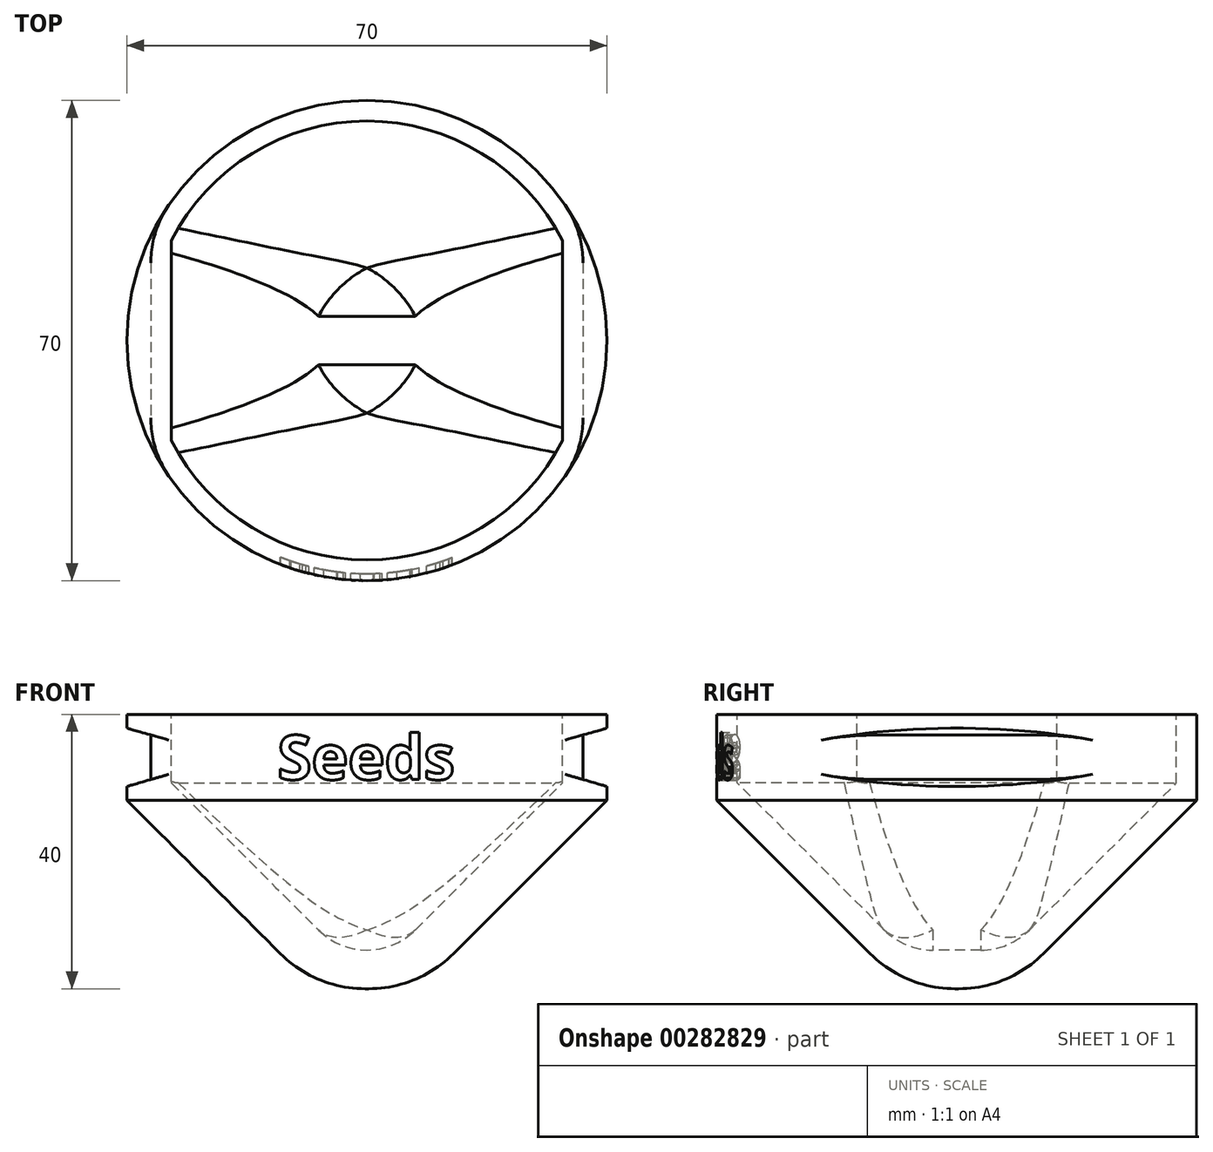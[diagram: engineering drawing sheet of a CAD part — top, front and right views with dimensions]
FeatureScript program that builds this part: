
annotation { "Feature Type Name" : "Feature", "Feature Type Description" : "" }
export const myFeature = defineFeature(function(context is Context, id is Id, definition is map)
    precondition{}
    {
        {
            var Q0;
            Q0=qCreatedBy(makeId("Top.planeOp"),FACE);
            var sketch = newSketch(context, id + "F0", { "sketchPlane" : qUnion([Q0])});
            skCircle(sketch, "E0", {"center": v(0, 0) * mm, "radius": 35 * mm});
            skSolve(sketch);
        }
        {
            var Q0;
            Q0=qSketchRegion(id+"F0",true);
            extrude(context, id + "F1", {"entities" : qUnion([Q0]), "depth" : 12.5 * mm});
        }
        {
            var Q0;
            Q0=qCreatedBy(makeId("Front.planeOp"),FACE);
            var sketch = newSketch(context, id + "F2", { "sketchPlane" : qUnion([Q0])});
            skText(sketch, "E1", { "text": "Seeds\n", "fontName": "OpenSans-Bold.ttf"});
            const initialGuessF2  = {"E1": [-0.01304, 0.003, 1, 0, 0.0065]};
            skSetInitialGuess(sketch, initialGuessF2);
            skSolve(sketch);
        }
        {
            var Q0;
            Q0=qSketchRegion(id+"F2",true);
            var Q1;
            Q1=makeQuery(id+"F1.opExtrude","SWEPT_FACE",FACE,{"disambiguationData":[OSD([sQuery(id+"F0.wireOp",EDGE,"E0")])]});
            extrude(context, id + "F3", {"entities" : qUnion([Q0]), "operationType" : NewBodyOperationType.REMOVE, "endBound" : BoundingType.THROUGH_ALL, "endBoundEntityFace" : qUnion([Q1]), "depth" : 25 * mm});
        }
        {
            var Q0;
            Q0=makeQuery(id+"F1.opExtrude","CAP_FACE",FACE,{"disambiguationData":[OSD([sQuery(id+"F0.wireOp",EDGE,"E0")])],"isStart":false});
            var sketch = newSketch(context, id + "F4", { "sketchPlane" : qUnion([Q0])});
            skCircle(sketch, "E2", {"center": v(0, 0) * mm, "radius": 34 * mm});
            skSolve(sketch);
        }
        {
            var Q0;
            Q0=qSketchRegion(id+"F4",true);
            var Q1;
            Q1=makeQuery(id+"F1.opExtrude","CAP_FACE",FACE,{"disambiguationData":[OSD([sQuery(id+"F0.wireOp",EDGE,"E0")])],"isStart":true});
            extrude(context, id + "F5", {"entities" : qUnion([Q0]), "operationType" : NewBodyOperationType.ADD, "endBound" : BoundingType.UP_TO_SURFACE, "oppositeDirection" : true, "endBoundEntityFace" : qUnion([Q1]), "depth" : 25 * mm});
        }
        {
            var Q0;
            Q0=qCreatedBy(makeId("Front.planeOp"),FACE);
            var sketch = newSketch(context, id + "F6", { "sketchPlane" : qUnion([Q0])});
            skLineSegment(sketch, "E3", {"start": v(-35, 10.5) * mm, "end": v(-35, 2) * mm});
            skLineSegment(sketch, "E4", {"start": v(-35, 2) * mm, "end": v(-31.5, 3) * mm});
            skLineSegment(sketch, "E5", {"start": v(-31.5, 3) * mm, "end": v(-31.5, 9.5) * mm});
            skLineSegment(sketch, "E6", {"start": v(-31.5, 9.5) * mm, "end": v(-35, 10.5) * mm});
            skLineSegment(sketch, "E7.MirrorCS", {"start": v(35, 10.5) * mm, "end": v(35, 2) * mm});
            skLineSegment(sketch, "E8.MirrorCS", {"start": v(31.5, 9.5) * mm, "end": v(35, 10.5) * mm});
            skLineSegment(sketch, "E9.MirrorCS", {"start": v(35, 2) * mm, "end": v(31.5, 3) * mm});
            skLineSegment(sketch, "E10.MirrorCS", {"start": v(31.5, 3) * mm, "end": v(31.5, 9.5) * mm});
            skSolve(sketch);
        }
        {
            var Q0;
            Q0=qSketchRegion(id+"F6",true);
            extrude(context, id + "F7", {"entities" : qUnion([Q0]), "operationType" : NewBodyOperationType.REMOVE, "endBound" : BoundingType.THROUGH_ALL, "oppositeDirection" : true, "depth" : 25 * mm, "hasSecondDirection" : true, "secondDirectionBound" : SecondDirectionBoundingType.THROUGH_ALL, "secondDirectionOppositeDirection" : false, "secondDirectionDepth" : 25 * mm});
        }
        {
            var Q0;
            {var subQ0=sQuery(id+"F0.wireOp",EDGE,"E0");Q0=makeQuery(id+"F7.boolean.opBoolean","INTERSECT",EDGE,{"disambiguationData":[OD(0.0)],"derivedFrom":[makeQuery(id+"F3.boolean.opBoolean","SPLIT",FACE,{"disambiguationData":[TD([makeQuery(id+"F1.opExtrude","CAP_FACE",FACE,{"disambiguationData":[OSD([subQ0])],"isStart":true})])],"derivedFrom":makeQuery(id+"F1.opExtrude","SWEPT_FACE",FACE,{"disambiguationData":[OSD([subQ0])]})}),makeQuery(id+"F7.opExtrude","SWEPT_FACE",FACE,{"disambiguationData":[OSD([sQuery(id+"F6.wireOp",EDGE,"E5")])]})]});}
            var Q1;
            {var subQ0=sQuery(id+"F0.wireOp",EDGE,"E0");Q1=makeQuery(id+"F7.boolean.opBoolean","INTERSECT",EDGE,{"disambiguationData":[OD(0.0)],"derivedFrom":[makeQuery(id+"F3.boolean.opBoolean","SPLIT",FACE,{"disambiguationData":[TD([makeQuery(id+"F1.opExtrude","CAP_FACE",FACE,{"disambiguationData":[OSD([subQ0])],"isStart":true})])],"derivedFrom":makeQuery(id+"F1.opExtrude","SWEPT_FACE",FACE,{"disambiguationData":[OSD([subQ0])]})}),makeQuery(id+"F7.opExtrude","SWEPT_FACE",FACE,{"disambiguationData":[OSD([sQuery(id+"F6.wireOp",EDGE,"E10.MirrorCS")])]})]});}
            var Q2;
            {var subQ0=sQuery(id+"F0.wireOp",EDGE,"E0");Q2=makeQuery(id+"F7.boolean.opBoolean","INTERSECT",EDGE,{"disambiguationData":[OD(1.0)],"derivedFrom":[makeQuery(id+"F3.boolean.opBoolean","SPLIT",FACE,{"disambiguationData":[TD([makeQuery(id+"F1.opExtrude","CAP_FACE",FACE,{"disambiguationData":[OSD([subQ0])],"isStart":true})])],"derivedFrom":makeQuery(id+"F1.opExtrude","SWEPT_FACE",FACE,{"disambiguationData":[OSD([subQ0])]})}),makeQuery(id+"F7.opExtrude","SWEPT_FACE",FACE,{"disambiguationData":[OSD([sQuery(id+"F6.wireOp",EDGE,"E10.MirrorCS")])]})]});}
            var Q3;
            {var subQ0=sQuery(id+"F0.wireOp",EDGE,"E0");Q3=makeQuery(id+"F7.boolean.opBoolean","INTERSECT",EDGE,{"disambiguationData":[OD(1.0)],"derivedFrom":[makeQuery(id+"F3.boolean.opBoolean","SPLIT",FACE,{"disambiguationData":[TD([makeQuery(id+"F1.opExtrude","CAP_FACE",FACE,{"disambiguationData":[OSD([subQ0])],"isStart":true})])],"derivedFrom":makeQuery(id+"F1.opExtrude","SWEPT_FACE",FACE,{"disambiguationData":[OSD([subQ0])]})}),makeQuery(id+"F7.opExtrude","SWEPT_FACE",FACE,{"disambiguationData":[OSD([sQuery(id+"F6.wireOp",EDGE,"E5")])]})]});}
            fillet(context, id + "F8", {"entities" : qUnion([Q0, Q1, Q2, Q3]), "radius" : 15 * mm, "tangentPropagation" : true, "allowEdgeOverflow" : false});
        }
        {
            var Q0;
            Q0=makeQuery(id+"F1.opExtrude","CAP_FACE",FACE,{"disambiguationData":[OSD([sQuery(id+"F0.wireOp",EDGE,"E0")])],"isStart":true});
            var sketch = newSketch(context, id + "F9", { "sketchPlane" : qUnion([Q0])});
            skCircle(sketch, "E11.0.0", {"center": v(0, 0) * mm, "radius": 35 * mm});
            skSolve(sketch);
        }
        {
            var Q0;
            Q0=qSketchRegion(id+"F9",true);
            extrude(context, id + "F10", {"entities" : qUnion([Q0]), "operationType" : NewBodyOperationType.ADD, "depth" : 27.5 * mm, "hasDraft" : true, "draftAngle" : 45 * degree, "draftPullDirection" : true});
        }
        {
            var Q0;
            Q0=makeQuery(id+"F1.opExtrude","CAP_FACE",FACE,{"disambiguationData":[OSD([sQuery(id+"F0.wireOp",EDGE,"E0")])],"isStart":false});
            var sketch = newSketch(context, id + "F11", { "sketchPlane" : qUnion([Q0])});
            skArc(sketch, "E12", {"start": v(-28.5, -14.55) * mm, "mid": v(0, -32) * mm, "end": v(28.5, -14.55) * mm});
            skLineSegment(sketch, "E13", {"start": v(-28.5, 14.55) * mm, "end": v(-28.5, -14.55) * mm});
            skLineSegment(sketch, "E14", {"start": v(28.5, 14.55) * mm, "end": v(28.5, -14.55) * mm});
            skArc(sketch, "E15.trimOffspring", {"start": v(28.5, 14.55) * mm, "mid": v(0, 32) * mm, "end": v(-28.5, 14.55) * mm});
            skSolve(sketch);
        }
        {
            var Q0;
            Q0=qSketchRegion(id+"F11",true);
            extrude(context, id + "F12", {"entities" : qUnion([Q0]), "operationType" : NewBodyOperationType.REMOVE, "oppositeDirection" : true, "depth" : 10 * mm});
        }
        {
            var Q0;
            Q0=makeQuery(id+"F12.boolean.opBoolean","COPY",FACE,{"derivedFrom":makeQuery(id+"F12.opExtrude","CAP_FACE",FACE,{"disambiguationData":[OSD([sQuery(id+"F11.wireOp",EDGE,"E12"),sQuery(id+"F11.wireOp",EDGE,"E13"),sQuery(id+"F11.wireOp",EDGE,"E14"),sQuery(id+"F11.wireOp",EDGE,"E15.trimOffspring")])],"isStart":false})});
            var sketch = newSketch(context, id + "F13", { "sketchPlane" : qUnion([Q0])});
            skArc(sketch, "E16.0", {"start": v(28.5, 14.55) * mm, "mid": v(0, 32) * mm, "end": v(-28.5, 14.55) * mm});
            skLineSegment(sketch, "E17.0", {"start": v(-28.5, 14.55) * mm, "end": v(-28.5, -14.55) * mm});
            skArc(sketch, "E17.1", {"start": v(-28.5, -14.55) * mm, "mid": v(0, -32) * mm, "end": v(28.5, -14.55) * mm});
            skLineSegment(sketch, "E17.2", {"start": v(28.5, 14.55) * mm, "end": v(28.5, -14.55) * mm});
            skSolve(sketch);
        }
        {
            var Q0;
            Q0=qSketchRegion(id+"F13",true);
            extrude(context, id + "F14", {"entities" : qUnion([Q0]), "operationType" : NewBodyOperationType.REMOVE, "endBound" : BoundingType.THROUGH_ALL, "oppositeDirection" : true, "depth" : 45 * mm, "hasDraft" : true, "draftAngle" : 45 * degree, "draftPullDirection" : true});
        }
        {
            var Q0;
            Q0=makeQuery(id+"F14.boolean.opBoolean","COPY",EDGE,{"derivedFrom":makeQuery(id+"F14.*.draft.opDraft","SPLIT",EDGE,{"derivedFrom":makeQuery(id+"F14.opExtrude","SWEPT_EDGE",EDGE,{"disambiguationData":[OSD([sQuery(id+"F13.wireOp",EDGE,"E16.0"),sQuery(id+"F13.wireOp",EDGE,"E17.0")])]})})});
            var Q1;
            {var subQ0=sQuery(id+"F13.wireOp",EDGE,"E17.2");var subQ1=sQuery(id+"F13.wireOp",EDGE,"E16.0");var subQ2=sQuery(id+"F13.wireOp",EDGE,"E17.0");var subQ3=sQuery(id+"F13.wireOp",EDGE,"E17.1");Q1=makeQuery(id+"F14.boolean.opBoolean","COPY",EDGE,{"derivedFrom":makeQuery(id+"F14.*.draft.opDraft","MERGE",EDGE,{"derivedFrom":[makeQuery(id+"F14.opExtrude","SWEPT_EDGE",EDGE,{"disambiguationData":[OSD([subQ2,subQ3])]}),makeQuery(id+"F14.opExtrude","SWEPT_EDGE",EDGE,{"disambiguationData":[OSD([subQ3,subQ0])]}),makeQuery(id+"F14.opExtrude","SWEPT_EDGE",EDGE,{"disambiguationData":[OSD([subQ1,subQ2])]}),makeQuery(id+"F14.opExtrude","SWEPT_EDGE",EDGE,{"disambiguationData":[OSD([subQ1,subQ0])]})]})});}
            var Q2;
            Q2=makeQuery(id+"F14.boolean.opBoolean","COPY",EDGE,{"derivedFrom":makeQuery(id+"F14.*.draft.opDraft","SPLIT",EDGE,{"derivedFrom":makeQuery(id+"F14.opExtrude","SWEPT_EDGE",EDGE,{"disambiguationData":[OSD([sQuery(id+"F13.wireOp",EDGE,"E16.0"),sQuery(id+"F13.wireOp",EDGE,"E17.2")])]})})});
            var Q3;
            Q3=makeQuery(id+"F14.boolean.opBoolean","COPY",EDGE,{"derivedFrom":makeQuery(id+"F14.*.draft.opDraft","SPLIT",EDGE,{"derivedFrom":makeQuery(id+"F14.opExtrude","SWEPT_EDGE",EDGE,{"disambiguationData":[OSD([sQuery(id+"F13.wireOp",EDGE,"E17.1"),sQuery(id+"F13.wireOp",EDGE,"E17.2")])]})})});
            var Q4;
            Q4=makeQuery(id+"F14.boolean.opBoolean","COPY",EDGE,{"derivedFrom":makeQuery(id+"F14.*.draft.opDraft","SPLIT",EDGE,{"derivedFrom":makeQuery(id+"F14.opExtrude","SWEPT_EDGE",EDGE,{"disambiguationData":[OSD([sQuery(id+"F13.wireOp",EDGE,"E17.0"),sQuery(id+"F13.wireOp",EDGE,"E17.1")])]})})});
            fillet(context, id + "F15", {"entities" : qUnion([Q0, Q1, Q2, Q3, Q4]), "radius" : 10 * mm, "allowEdgeOverflow" : false});
        }
        {
            var Q0;
            Q0=makeQuery(id+"F10.opExtrude","CAP_EDGE",EDGE,{"disambiguationData":[OSD([sQuery(id+"F9.wireOp",EDGE,"E11.0.0")])],"isStart":false});
            fillet(context, id + "F16", {"entities" : qUnion([Q0]), "radius" : 17.5 * mm, "tangentPropagation" : true, "allowEdgeOverflow" : false});
        }
    });
